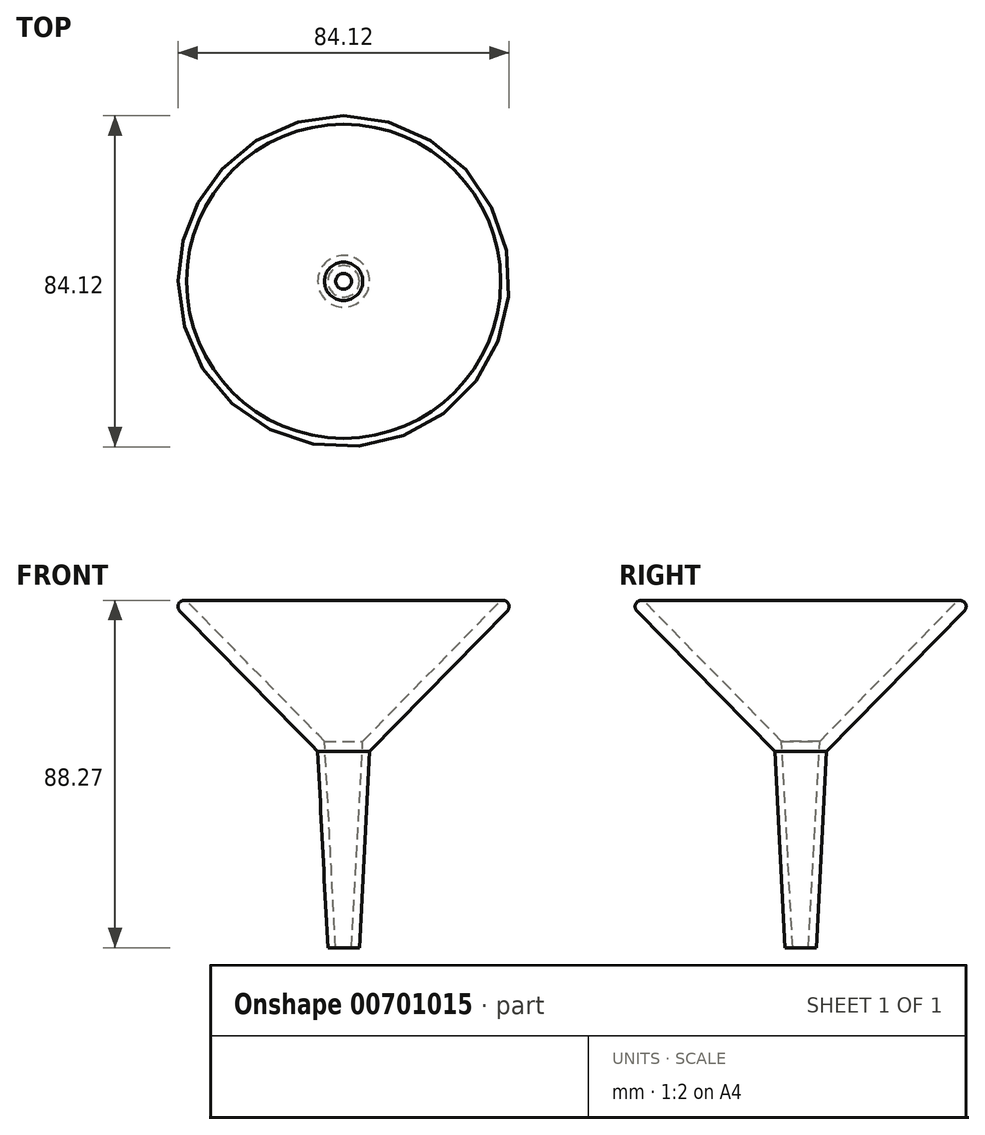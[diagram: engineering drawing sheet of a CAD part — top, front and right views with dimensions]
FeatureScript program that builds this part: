
annotation { "Feature Type Name" : "Feature", "Feature Type Description" : "" }
export const myFeature = defineFeature(function(context is Context, id is Id, definition is map)
    precondition{}
    {
        {
            var Q0;
            Q0=qCreatedBy(makeId("Front.planeOp"),FACE);
            var sketch = newSketch(context, id + "F0", { "sketchPlane" : qUnion([Q0])});
            skLineSegment(sketch, "E0", {"start": v(4.86, 52.47) * mm, "end": v(39.9, 88.15) * mm});
            skLineSegment(sketch, "E1", {"start": v(6.58, 49.93) * mm, "end": v(41.6, 85.6) * mm});
            skArc(sketch, "E2", {"start": v(41.6, 85.6) * mm, "mid": v(41.79, 87.58) * mm, "end": v(39.9, 88.15) * mm});
            skLineSegment(sketch, "E3", {"start": v(4.86, 52.47) * mm, "end": v(2, 0) * mm});
            skLineSegment(sketch, "E4", {"start": v(6.58, 49.93) * mm, "end": v(4, 0) * mm});
            skLineSegment(sketch, "E5", {"start": v(2, 0) * mm, "end": v(4, 0) * mm});
            skLineSegment(sketch, "E6", {"start": v(0, 0) * mm, "end": v(0, 20.74) * mm});
            skSolve(sketch);
        }
        {
            var Q0;
            Q0=qSketchRegion(id+"F0",true);
            var Q1;
            Q1=sQuery(id+"F0.wireOp",EDGE,"E6");
            revolve(context, id + "F1", {"entities" : qUnion([Q0]), "axis" : qUnion([Q1]), "revolveType" : RevolveType.FULL});
        }
    });
